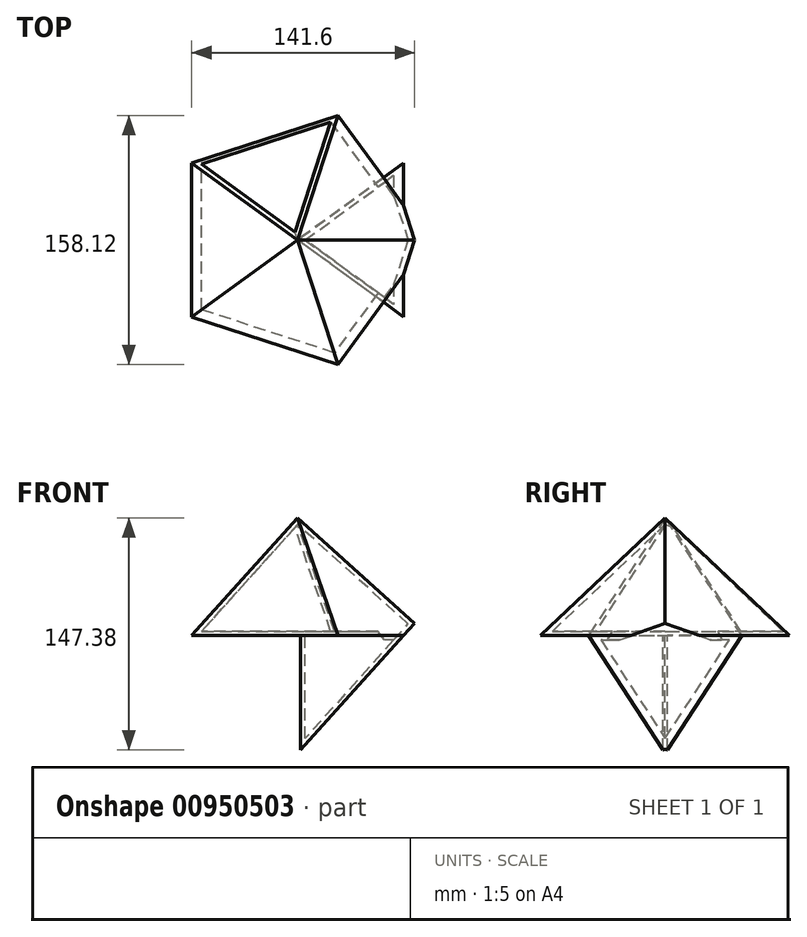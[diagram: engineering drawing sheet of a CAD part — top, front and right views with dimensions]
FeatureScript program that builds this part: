
annotation { "Feature Type Name" : "Feature", "Feature Type Description" : "" }
export const myFeature = defineFeature(function(context is Context, id is Id, definition is map)
    precondition{}
    {
        {
            var Q0;
            Q0=qCreatedBy(makeId("Front.planeOp"),FACE);
            var sketch = newSketch(context, id + "F0", { "sketchPlane" : qUnion([Q0])});
            skLineSegment(sketch, "E0", {"start": v(-33.62, 0) * mm, "end": v(0, 37.38) * mm, "construction": true});
            skLineSegment(sketch, "E1", {"start": v(0, 37.38) * mm, "end": v(0, 0) * mm, "construction": true});
            skLineSegment(sketch, "E2", {"start": v(0, 37.38) * mm, "end": v(41.56, 0) * mm, "construction": true});
            skCircle(sketch, "E3.cCircle", {"center": v(0, 0) * mm, "radius": 33.62 * mm, "construction": true});
            skLineSegment(sketch, "E3.0", {"start": v(-33.62, -24.43) * mm, "end": v(-33.62, 24.43) * mm, "construction": true});
            skLineSegment(sketch, "E3.1", {"start": v(-33.62, 24.43) * mm, "end": v(12.84, 39.53) * mm, "construction": true});
            skLineSegment(sketch, "E3.2", {"start": v(12.84, 39.53) * mm, "end": v(41.56, 0) * mm, "construction": true});
            skLineSegment(sketch, "E3.3", {"start": v(41.56, 0) * mm, "end": v(12.84, -39.53) * mm, "construction": true});
            skLineSegment(sketch, "E3.4", {"start": v(12.84, -39.53) * mm, "end": v(-33.62, -24.43) * mm, "construction": true});
            skPoint(sketch, "E3.0.midPoint", {"position": v(-33.62, 0) * mm});
            skLineSegment(sketch, "E4", {"start": v(0, 0) * mm, "end": v(0, -37.38) * mm, "construction": true});
            skSolve(sketch);
        }
        {
            var Q0;
            Q0=qCreatedBy(makeId("Top.planeOp"),FACE);
            var sketch = newSketch(context, id + "F1", { "sketchPlane" : qUnion([Q0])});
            skCircle(sketch, "E5.cCircle", {"center": v(0, 0) * mm, "radius": 33.62 * mm, "construction": true});
            skLineSegment(sketch, "E5.0", {"start": v(-33.62, -24.43) * mm, "end": v(-33.62, 24.43) * mm, "construction": true});
            skLineSegment(sketch, "E5.1", {"start": v(-33.62, 24.43) * mm, "end": v(12.84, 39.53) * mm, "construction": true});
            skLineSegment(sketch, "E5.2", {"start": v(12.84, 39.53) * mm, "end": v(41.56, 0) * mm, "construction": true});
            skLineSegment(sketch, "E5.3", {"start": v(41.56, 0) * mm, "end": v(12.84, -39.53) * mm, "construction": true});
            skLineSegment(sketch, "E5.4", {"start": v(12.84, -39.53) * mm, "end": v(-33.62, -24.43) * mm, "construction": true});
            skPoint(sketch, "E5.0.midPoint", {"position": v(-33.62, 0) * mm});
            skLineSegment(sketch, "E6.0", {"start": v(33.62, 24.43) * mm, "end": v(33.62, -24.43) * mm, "construction": true});
            skLineSegment(sketch, "E6.1", {"start": v(33.62, -24.43) * mm, "end": v(-12.84, -39.53) * mm, "construction": true});
            skLineSegment(sketch, "E6.2", {"start": v(-12.84, -39.53) * mm, "end": v(-41.56, 0) * mm, "construction": true});
            skLineSegment(sketch, "E6.3", {"start": v(-41.56, 0) * mm, "end": v(-12.84, 39.53) * mm, "construction": true});
            skLineSegment(sketch, "E6.4", {"start": v(-12.84, 39.53) * mm, "end": v(33.62, 24.43) * mm, "construction": true});
            skPoint(sketch, "E6.0.midPoint", {"position": v(33.62, 0) * mm});
            skSolve(sketch);
        }
        {
            var Q0;
            Q0=sQuery(id+"F0.wireOp",VERTEX,"E0.end");
            var Q1;
            Q1=sQuery(id+"F1.wireOp",VERTEX,"E5.0.end");
            var Q2;
            Q2=sQuery(id+"F1.wireOp",VERTEX,"E5.0.start");
            cPlane(context, id + "F2", {"entities" : qUnion([Q0, Q1, Q2]), "cplaneType" : CPlaneType.THREE_POINT, "offset" : 25 * mm, "width" : 150 * mm, "height" : 150 * mm});
        }
        {
            var Q0;
            Q0=qCreatedBy(id+"F2.planeOp",FACE);
            var sketch = newSketch(context, id + "F3", { "sketchPlane" : qUnion([Q0])});
            skLineSegment(sketch, "E7.0", {"start": v(-24.43, -22.49) * mm, "end": v(24.43, -22.49) * mm});
            skLineSegment(sketch, "E8", {"start": v(24.43, -22.49) * mm, "end": v(0, 27.8) * mm});
            skLineSegment(sketch, "E9", {"start": v(0, 27.8) * mm, "end": v(-24.43, -22.49) * mm});
            skSolve(sketch);
        }
        {
            var Q0;
            Q0=makeQuery(id+"F3.imprint","IMPRINT",FACE,{"disambiguationData":[TD([[makeQuery(id+"F3.imprint","IMPRINT",EDGE,{"derivedFrom":sQuery(id+"F3.wireOp",EDGE,"E7.0")}),1.0]])]});
            var Q1;
            Q1=qCreatedBy(makeId("Origin.pointOp"),VERTEX);
            loft(context, id + "F4", {"sheetProfilesArray" : [{ "sheetProfileEntities" : qUnion([Q0]) }, { "sheetProfileEntities" : qUnion([Q1]) }]});
        }
        {
            var Q0;
            Q0=makeQuery(id+"F4.opLoft","SWEPT_BODY",BODY,{"disambiguationData":[OSD([dummyQuery(id+"Origin.pointOp",VERTEX),makeQuery(id+"F3.imprint","IMPRINT",FACE,{"disambiguationData":[TD([[makeQuery(id+"F3.imprint","IMPRINT",EDGE,{"derivedFrom":sQuery(id+"F3.wireOp",EDGE,"E7.0")}),1.0]])]})])]});
            var Q1;
            Q1=sQuery(id+"F0.wireOp",EDGE,"E1");
            circularPattern(context, id + "F5", {"operationType" : NewBodyOperationType.ADD, "entities" : qUnion([Q0]), "axis" : qUnion([Q1]), "angle" : 360 * degree, "instanceCount" : 5, "equalSpace" : true});
        }
        {
            var Q0;
            Q0=sQuery(id+"F1.wireOp",VERTEX,"E6.0.end");
            var Q1;
            Q1=sQuery(id+"F1.wireOp",VERTEX,"E6.0.start");
            var Q2;
            Q2=sQuery(id+"F0.wireOp",VERTEX,"E4.end");
            cPlane(context, id + "F6", {"entities" : qUnion([Q0, Q1, Q2]), "cplaneType" : CPlaneType.THREE_POINT, "offset" : 25 * mm, "width" : 150 * mm, "height" : 150 * mm});
        }
        {
            var Q0;
            Q0=qCreatedBy(id+"F6.planeOp",FACE);
            var sketch = newSketch(context, id + "F7", { "sketchPlane" : qUnion([Q0])});
            skLineSegment(sketch, "E10.0", {"start": v(24.43, 22.49) * mm, "end": v(-24.43, 22.49) * mm});
            skLineSegment(sketch, "E11", {"start": v(-24.43, 22.49) * mm, "end": v(0, -27.8) * mm});
            skLineSegment(sketch, "E12", {"start": v(0, -27.8) * mm, "end": v(24.43, 22.49) * mm});
            skSolve(sketch);
        }
        {
            var Q1;
            Q1=makeQuery(id+"F7.imprint","IMPRINT",FACE,{"disambiguationData":[TD([[makeQuery(id+"F7.imprint","IMPRINT",EDGE,{"derivedFrom":sQuery(id+"F7.wireOp",EDGE,"E10.0")}),1.0]])]});
            var Q2;
            Q2=sQuery(id+"F0.wireOp",VERTEX,"E1.end");
            loft(context, id + "F8", {"operationType" : NewBodyOperationType.ADD, "sheetProfilesArray" : [{ "sheetProfileEntities" : qUnion([Q1]) }, { "sheetProfileEntities" : qUnion([Q2]) }]});
        }
        {
            var Q0;
            Q0=makeQuery(id+"F4.opLoft","CAP_FACE",FACE,{"disambiguationData":[OSD([makeQuery(id+"F3.imprint","IMPRINT",FACE,{"disambiguationData":[TD([[makeQuery(id+"F3.imprint","IMPRINT",EDGE,{"derivedFrom":sQuery(id+"F3.wireOp",EDGE,"E7.0")}),1.0]])]})])],"isStart":true});
            var sketch = newSketch(context, id + "F9", { "sketchPlane" : qUnion([Q0])});
            skLineSegment(sketch, "E13", {"start": v(-27, -27.8) * mm, "end": v(0, 27.8) * mm});
            skLineSegment(sketch, "E14", {"start": v(0, 27.8) * mm, "end": v(27, -27.8) * mm});
            skLineSegment(sketch, "E15", {"start": v(27, -27.8) * mm, "end": v(-27, -27.8) * mm});
            skSolve(sketch);
        }
        {
            var Q0;
            {var subQ21=sQuery(id+"F9.wireOp",EDGE,"E14");var subQ23=sQuery(id+"F9.wireOp",EDGE,"E13");var subQ24=makeQuery(id+"F9.imprint","INTERSECT",VERTEX,{"derivedFrom":[subQ23,subQ21]});Q0=makeQuery(id+"F9.imprint","IMPRINT",FACE,{"disambiguationData":[TD([[makeQuery(id+"F9.imprint","IMPRINT",EDGE,{"disambiguationData":[TD([[subQ24,-1.0]])],"derivedFrom":subQ21}),-1.0]])]});}
            var Q1;
            {var subQ21=sQuery(id+"F9.wireOp",EDGE,"E15");Q1=makeQuery(id+"F9.imprint","IMPRINT",FACE,{"disambiguationData":[TD([[makeQuery(id+"F9.imprint","IMPRINT",EDGE,{"derivedFrom":subQ21}),-1.0]])]});}
            extrude(context, id + "F10", {"entities" : qUnion([Q0, Q1]), "operationType" : NewBodyOperationType.REMOVE, "depth" : 25 * mm, "offsetDistance" : 25 * mm});
        }
        {
            var Q0;
            Q0=makeQuery(id+"F8.opLoft","CAP_FACE",FACE,{"disambiguationData":[OSD([makeQuery(id+"F7.imprint","IMPRINT",FACE,{"disambiguationData":[TD([[makeQuery(id+"F7.imprint","IMPRINT",EDGE,{"derivedFrom":sQuery(id+"F7.wireOp",EDGE,"E10.0")}),1.0]])]})])],"isStart":true});
            var sketch = newSketch(context, id + "F11", { "sketchPlane" : qUnion([Q0])});
            skLineSegment(sketch, "E16", {"start": v(-27, 27.8) * mm, "end": v(0, -27.8) * mm});
            skLineSegment(sketch, "E17", {"start": v(0, -27.8) * mm, "end": v(27, 27.8) * mm});
            skLineSegment(sketch, "E18", {"start": v(27, 27.8) * mm, "end": v(-27, 27.8) * mm});
            skSolve(sketch);
        }
        {
            var Q0;
            {var subQ0=sQuery(id+"F11.wireOp",EDGE,"E18");Q0=makeQuery(id+"F11.imprint","IMPRINT",FACE,{"disambiguationData":[TD([[makeQuery(id+"F11.imprint","IMPRINT",EDGE,{"derivedFrom":subQ0}),1.0]])]});}
            var Q1;
            {var subQ4=sQuery(id+"F7.wireOp",EDGE,"E10.0");var subQ5=makeQuery(id+"F7.imprint","IMPRINT",EDGE,{"derivedFrom":subQ4});var subQ8=makeQuery(id+"F8.opLoft","CAP_FACE",FACE,{"disambiguationData":[OSD([makeQuery(id+"F7.imprint","IMPRINT",FACE,{"disambiguationData":[TD([[subQ5,1.0]])]})])],"isStart":true});var subQ12=sQuery(id+"F9.wireOp",EDGE,"E15");var subQ13=sQuery(id+"F9.wireOp",EDGE,"E14");var subQ14=sQuery(id+"F9.wireOp",EDGE,"E13");var subQ15=makeQuery(id+"FLSPnottfK7hvsf_1.2.F10.boolean.opBoolean","INTERSECT",EDGE,{"derivedFrom":[subQ8,makeQuery(id+"FLSPnottfK7hvsf_1.2.F10.opExtrude","CAP_FACE",FACE,{"disambiguationData":[OSD([subQ14,subQ13,subQ12])],"isStart":true})]});Q1=makeQuery(id+"F11.imprint","IMPRINT",FACE,{"disambiguationData":[TD([[makeQuery(id+"F11.imprint","IMPRINT",EDGE,{"derivedFrom":subQ15}),1.0]])]});}
            extrude(context, id + "F12", {"entities" : qUnion([Q0, Q1]), "operationType" : NewBodyOperationType.REMOVE, "depth" : 25 * mm, "offsetDistance" : 25 * mm});
        }
        {
            var Q0;
            Q0=makeQuery(id+"F4.opLoft","SWEPT_BODY",BODY,{"disambiguationData":[OSD([dummyQuery(id+"Origin.pointOp",VERTEX),makeQuery(id+"F3.imprint","IMPRINT",FACE,{"disambiguationData":[TD([[makeQuery(id+"F3.imprint","IMPRINT",EDGE,{"derivedFrom":sQuery(id+"F3.wireOp",EDGE,"E7.0")}),1.0]])]})])]});
            var Q1;
            Q1=qCreatedBy(makeId("Origin.pointOp"),VERTEX);
            transform(context, id + "F13", {"entities" : qUnion([Q0]), "transformType" : TransformType.SCALE_UNIFORMLY, "scale" : 2, "scalePoint" : qUnion([Q1]), "makeCopy" : false});
        }
        {
            var Q0;
            Q0=makeQuery(id+"FLSPnottfK7hvsf_1.1.F10.boolean.opBoolean","MERGE",FACE,{"derivedFrom":[makeQuery(id+"F5.opPattern","COPY",FACE,{"derivedFrom":makeQuery(id+"F4.opLoft","CAP_FACE",FACE,{"disambiguationData":[OSD([makeQuery(id+"F3.imprint","IMPRINT",FACE,{"disambiguationData":[TD([[makeQuery(id+"F3.imprint","IMPRINT",EDGE,{"derivedFrom":sQuery(id+"F3.wireOp",EDGE,"E7.0")}),1.0]])]})])],"isStart":true}),"instanceName":"1"})],"fromTools":[makeQuery(id+"FLSPnottfK7hvsf_1.1.F10.opExtrude","CAP_FACE",FACE,{"disambiguationData":[OSD([sQuery(id+"F9.wireOp",EDGE,"E13"),sQuery(id+"F9.wireOp",EDGE,"E14"),sQuery(id+"F9.wireOp",EDGE,"E15")])],"isStart":true})]});
            shell(context, id + "F14", {"entities" : qUnion([Q0]), "thickness" : 2.8 * mm});
        }
        {
            var Q0;
            Q0=qCreatedBy(makeId("Top.planeOp"),FACE);
            var sketch = newSketch(context, id + "F15", { "sketchPlane" : qUnion([Q0])});
            skCircle(sketch, "E19", {"center": v(0, 0) * mm, "radius": 2.4 * mm});
            skSolve(sketch);
        }
        {
            var Q0;
            Q0 = qSketchRegion(id + "F15", true);
            extrude(context, id + "F16", {"entities" : qUnion([Q0]), "operationType" : NewBodyOperationType.REMOVE, "endBound" : BoundingType.THROUGH_ALL, "oppositeDirection" : true, "depth" : 25 * mm, "offsetDistance" : 25 * mm});
        }
    });
